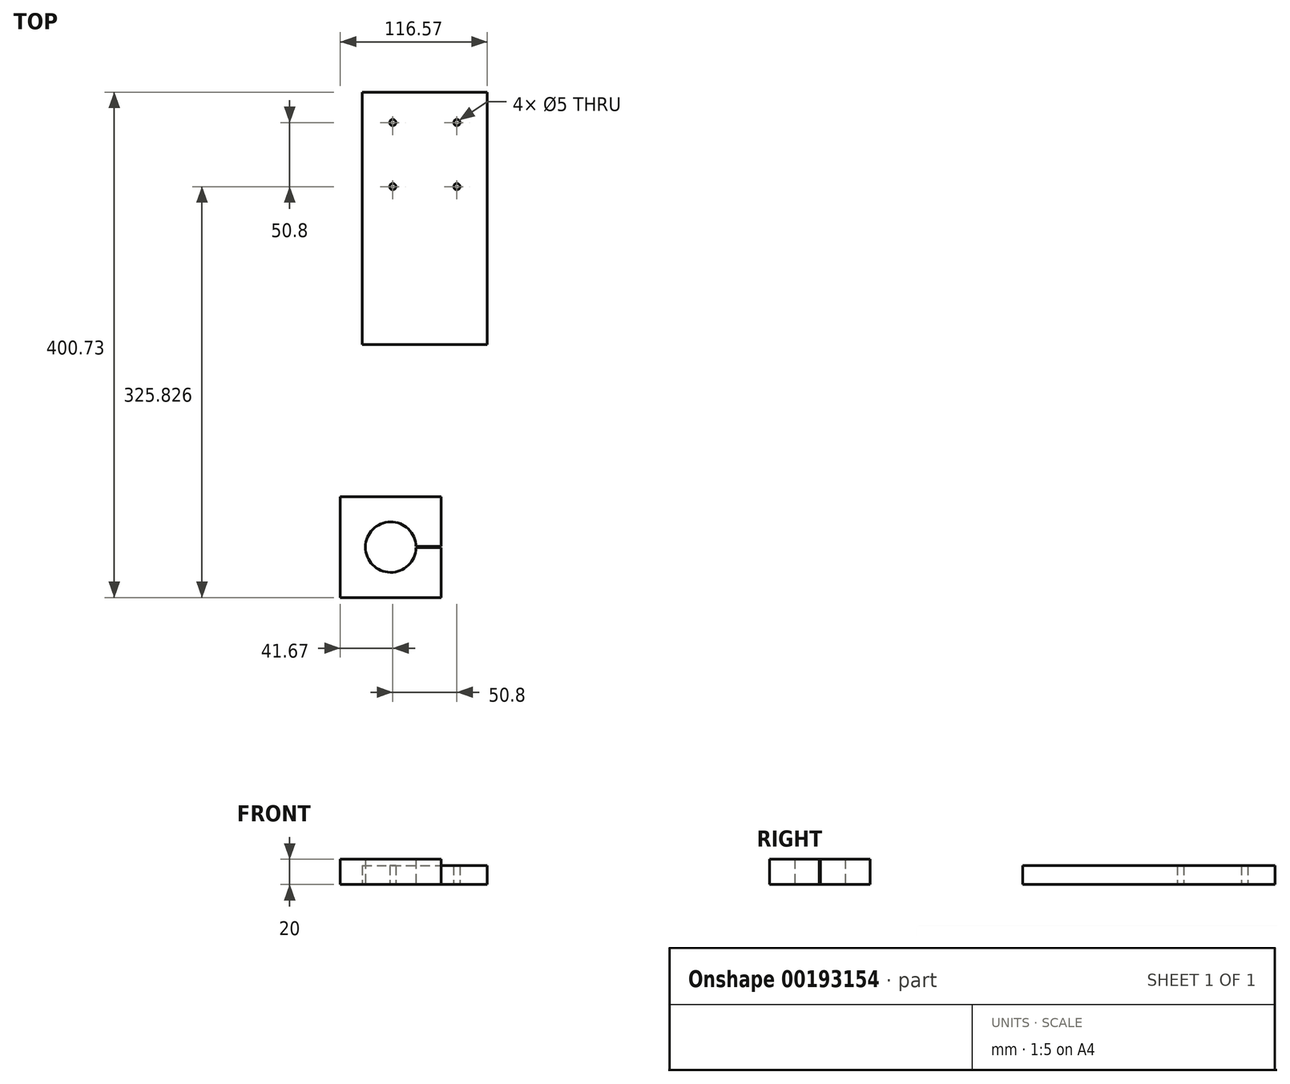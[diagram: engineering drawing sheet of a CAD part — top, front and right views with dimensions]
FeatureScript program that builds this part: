
annotation { "Feature Type Name" : "Feature", "Feature Type Description" : "" }
export const myFeature = defineFeature(function(context is Context, id is Id, definition is map)
    precondition{}
    {
        {
            var Q0;
            Q0=qCreatedBy(makeId("Top.planeOp"),FACE);
            var sketch = newSketch(context, id + "F0", { "sketchPlane" : qUnion([Q0])});
            skLineSegment(sketch, "E0.bottom", {"start": v(-98.8, 194.97) * mm, "end": v(0.2, 194.97) * mm});
            skLineSegment(sketch, "E0.top", {"start": v(-98.8, -5.03) * mm, "end": v(0.2, -5.03) * mm});
            skLineSegment(sketch, "E0.left", {"start": v(-98.8, 194.97) * mm, "end": v(-98.8, -5.03) * mm});
            skLineSegment(sketch, "E0.right", {"start": v(0.2, 194.97) * mm, "end": v(0.2, -5.03) * mm});
            skCircle(sketch, "E1", {"center": v(-74.7, 170.87) * mm, "radius": 2.5 * mm});
            skCircle(sketch, "E2.MirrorC", {"center": v(-23.9, 170.87) * mm, "radius": 2.5 * mm});
            skCircle(sketch, "E3.MirrorC", {"center": v(-23.9, 120.07) * mm, "radius": 2.5 * mm});
            skCircle(sketch, "E4.MirrorC", {"center": v(-74.7, 120.07) * mm, "radius": 2.5 * mm});
            skSolve(sketch);
        }
        {
            var Q0;
            Q0 = qSketchRegion(id + "F0", true);
            extrude(context, id + "F1", {"entities" : qUnion([Q0]), "depth" : 15 * mm});
        }
        {
            var Q0;
            Q0=qCreatedBy(makeId("Top.planeOp"),FACE);
            var sketch = newSketch(context, id + "F2", { "sketchPlane" : qUnion([Q0])});
            skLineSegment(sketch, "E5.bottom", {"start": v(-116.37, -125.76) * mm, "end": v(-36.37, -125.76) * mm});
            skLineSegment(sketch, "E5.top", {"start": v(-116.37, -205.76) * mm, "end": v(-36.37, -205.76) * mm});
            skLineSegment(sketch, "E5.left", {"start": v(-116.37, -125.76) * mm, "end": v(-116.37, -205.76) * mm});
            skLineSegment(sketch, "E5.right", {"start": v(-36.37, -125.76) * mm, "end": v(-36.37, -165.26) * mm});
            skLineSegment(sketch, "E6", {"start": v(-76.37, -125.76) * mm, "end": v(-76.37, -205.76) * mm, "construction": true});
            skArc(sketch, "E7", {"start": v(-56.37, -165.26) * mm, "mid": v(-96.37, -165.76) * mm, "end": v(-56.37, -166.26) * mm});
            skLineSegment(sketch, "E8", {"start": v(-36.37, -165.26) * mm, "end": v(-56.37, -165.26) * mm});
            skLineSegment(sketch, "E9", {"start": v(-56.37, -166.26) * mm, "end": v(-36.37, -166.26) * mm});
            skPoint(sketch, "E10.start.orphan", {"position": v(-36.37, -165.76) * mm});
            skLineSegment(sketch, "E11.trimOffspring", {"start": v(-36.37, -166.26) * mm, "end": v(-36.37, -205.76) * mm});
            skSolve(sketch);
        }
        {
            var Q0;
            Q0 = qSketchRegion(id + "F2", true);
            extrude(context, id + "F3", {"entities" : qUnion([Q0]), "depth" : 20 * mm});
        }
    });
